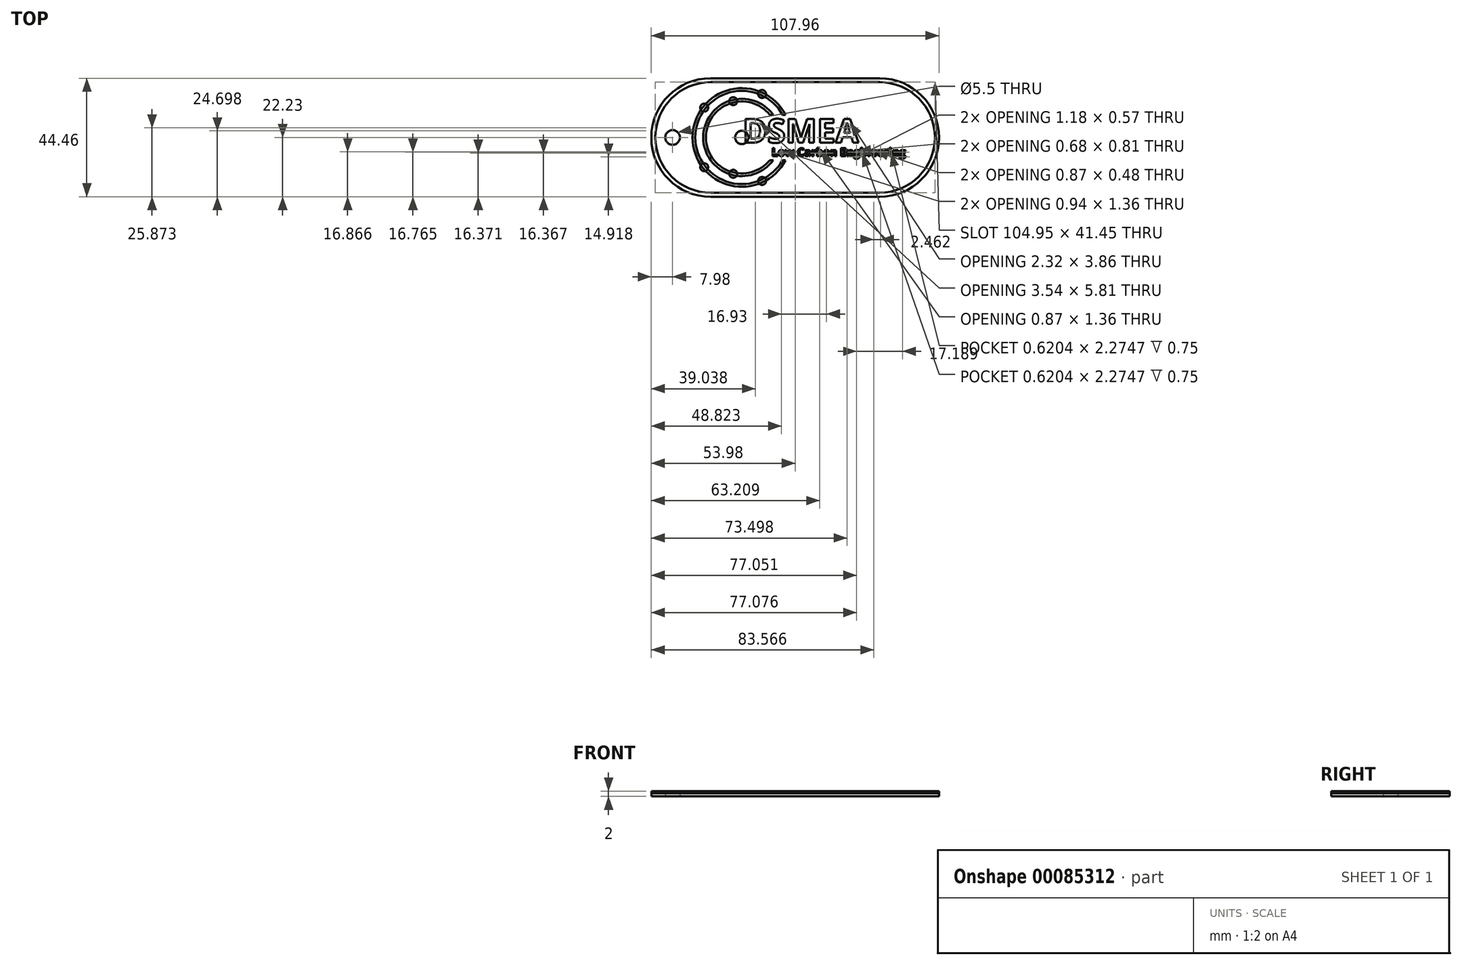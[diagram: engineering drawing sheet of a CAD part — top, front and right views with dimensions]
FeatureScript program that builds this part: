
annotation { "Feature Type Name" : "Feature", "Feature Type Description" : "" }
export const myFeature = defineFeature(function(context is Context, id is Id, definition is map)
    precondition{}
    {
        {
            var Q0;
            Q0=qCreatedBy(makeId("Top.planeOp"),FACE);
            var sketch = newSketch(context, id + "F0", { "sketchPlane" : qUnion([Q0])});
            skLineSegment(sketch, "E0.bottom", {"start": v(31.75, 22.22) * mm, "end": v(-31.75, 22.22) * mm});
            skLineSegment(sketch, "E0.top", {"start": v(31.75, -22.23) * mm, "end": v(-31.75, -22.23) * mm});
            skPoint(sketch, "E0.middle", {"position": v(0, 0) * mm});
            skArc(sketch, "E1", {"start": v(31.75, -22.23) * mm, "mid": v(53.98, 0) * mm, "end": v(31.75, 22.23) * mm});
            skArc(sketch, "E2", {"start": v(-31.75, 22.23) * mm, "mid": v(-53.98, 0) * mm, "end": v(-31.75, -22.23) * mm});
            skSolve(sketch);
        }
        {
            var Q0;
            Q0=qSketchRegion(id+"F0",true);
            extrude(context, id + "F1", {"entities" : qUnion([Q0]), "depth" : 2 * mm});
        }
        {
            var Q0;
            Q0=qCreatedBy(makeId("Top.planeOp"),FACE);
            cPlane(context, id + "F2", {"entities" : qUnion([Q0]), "cplaneType" : CPlaneType.OFFSET, "offset" : 1.25 * mm, "width" : 150 * mm, "height" : 150 * mm});
        }
        {
            var Q0;
            Q0=qCreatedBy(id+"F2.planeOp",FACE);
            var sketch = newSketch(context, id + "F3", { "sketchPlane" : qUnion([Q0])});
            skArc(sketch, "E3", {"start": v(-31.75, 22.23) * mm, "mid": v(-53.98, 0) * mm, "end": v(-31.75, -22.23) * mm});
            skArc(sketch, "E4.0", {"start": v(-31.75, 20.73) * mm, "mid": v(-52.48, 0) * mm, "end": v(-31.75, -20.73) * mm});
            skArc(sketch, "E5.MirrorC", {"start": v(31.75, 22.23) * mm, "mid": v(53.98, 0) * mm, "end": v(31.75, -22.23) * mm});
            skArc(sketch, "E6.MirrorC", {"start": v(31.75, 20.73) * mm, "mid": v(52.48, 0) * mm, "end": v(31.75, -20.73) * mm});
            skLineSegment(sketch, "E7", {"start": v(-31.75, -22.23) * mm, "end": v(31.75, -22.23) * mm});
            skLineSegment(sketch, "E8.MirrorCS", {"start": v(-31.75, 22.23) * mm, "end": v(31.75, 22.23) * mm});
            skLineSegment(sketch, "E9.0", {"start": v(-31.75, 20.73) * mm, "end": v(31.75, 20.73) * mm});
            skLineSegment(sketch, "E10.MirrorCS", {"start": v(-31.75, -20.73) * mm, "end": v(31.75, -20.73) * mm});
            skSolve(sketch);
        }
        {
            var Q0;
            Q0=qSketchRegion(id+"F3",true);
            extrude(context, id + "F4", {"entities" : qUnion([Q0]), "depth" : .75 * mm});
        }
        {
            var Q0;
            Q0=qCreatedBy(id+"F2.planeOp",FACE);
            var sketch = newSketch(context, id + "F5", { "sketchPlane" : qUnion([Q0])});
            skArc(sketch, "E11", {"start": v(-3.57, 8.5) * mm, "mid": v(-38.5, 0) * mm, "end": v(-3.57, -8.5) * mm});
            skArc(sketch, "E12", {"start": v(-4.7, 8.5) * mm, "mid": v(-37.5, 0) * mm, "end": v(-4.7, -8.5) * mm});
            skLineSegment(sketch, "E13.bottom", {"start": v(-3.57, 8.5) * mm, "end": v(-4.7, 8.5) * mm});
            skLineSegment(sketch, "E13.top", {"start": v(-3.57, -8.5) * mm, "end": v(-4.7, -8.5) * mm});
            skPoint(sketch, "E13.middle", {"position": v(0, 0) * mm});
            skSolve(sketch);
        }
        {
            var Q0;
            Q0=qSketchRegion(id+"F5",true);
            extrude(context, id + "F6", {"entities" : qUnion([Q0]), "depth" : .75 * mm});
        }
        {
            var Q0;
            Q0=qCreatedBy(id+"F2.planeOp",FACE);
            var sketch = newSketch(context, id + "F7", { "sketchPlane" : qUnion([Q0])});
            skArc(sketch, "E14", {"start": v(-8.25, 8.5) * mm, "mid": v(-34.5, 0) * mm, "end": v(-8.25, -8.5) * mm});
            skArc(sketch, "E15", {"start": v(-9.51, 8.5) * mm, "mid": v(-33.5, 0) * mm, "end": v(-9.51, -8.5) * mm});
            skLineSegment(sketch, "E16.bottom", {"start": v(-8.25, 8.5) * mm, "end": v(-9.51, 8.5) * mm});
            skLineSegment(sketch, "E16.top", {"start": v(-8.25, -8.5) * mm, "end": v(-9.51, -8.5) * mm});
            skPoint(sketch, "E16.middle", {"position": v(0, 0) * mm});
            skSolve(sketch);
        }
        {
            var Q0;
            Q0=qSketchRegion(id+"F7",true);
            extrude(context, id + "F8", {"entities" : qUnion([Q0]), "depth" : .75 * mm});
        }
        {
            var Q0;
            Q0=qCreatedBy(id+"F2.planeOp",FACE);
            var sketch = newSketch(context, id + "F9", { "sketchPlane" : qUnion([Q0])});
            skCircle(sketch, "E17", {"center": v(-20, 0) * mm, "radius": 2.5 * mm});
            skCircle(sketch, "E18", {"center": v(-20, 0) * mm, "radius": 18 * mm, "construction": true});
            skCircle(sketch, "E19", {"center": v(-20, 0) * mm, "radius": 14 * mm, "construction": true});
            skLineSegment(sketch, "E20", {"start": v(-20, 0) * mm, "end": v(-12.4, 16.31) * mm, "construction": true});
            skLineSegment(sketch, "E21", {"start": v(-20, 0) * mm, "end": v(-12.4, -16.31) * mm, "construction": true});
            skCircle(sketch, "E22", {"center": v(-12.4, 16.31) * mm, "radius": 1.5 * mm});
            skCircle(sketch, "E23.1.0", {"center": v(-34.12, 11.16) * mm, "radius": 1.5 * mm});
            skCircle(sketch, "E23.2.0", {"center": v(-34.12, -11.16) * mm, "radius": 1.5 * mm});
            skCircle(sketch, "E23.3.0", {"center": v(-12.4, -16.31) * mm, "radius": 1.5 * mm});
            skLineSegment(sketch, "E24", {"start": v(-34.12, 11.16) * mm, "end": v(-20, 0) * mm, "construction": true});
            skLineSegment(sketch, "E25", {"start": v(-23.23, 13.62) * mm, "end": v(-20, 0) * mm, "construction": true});
            skCircle(sketch, "E26", {"center": v(-23.23, 13.62) * mm, "radius": 1.5 * mm});
            skCircle(sketch, "E27.MirrorC", {"center": v(-23.23, -13.62) * mm, "radius": 1.5 * mm});
            skSolve(sketch);
        }
        {
            var Q0;
            Q0=qSketchRegion(id+"F9",true);
            extrude(context, id + "F10", {"entities" : qUnion([Q0]), "depth" : .75 * mm});
        }
        {
            var Q0;
            Q0=qCreatedBy(id+"F2.planeOp",FACE);
            var sketch = newSketch(context, id + "F11", { "sketchPlane" : qUnion([Q0])});
            skText(sketch, "E28", { "text": "DSMEA", "fontName": "OpenSans-Bold.ttf"});
            const initialGuessF11  = {"E28": [-0.01973, -0.002, 1, 0, 0.009]};
            skSetInitialGuess(sketch, initialGuessF11);
            skSolve(sketch);
        }
        {
            var Q0;
            Q0=qSketchRegion(id+"F11",true);
            extrude(context, id + "F12", {"entities" : qUnion([Q0]), "depth" : .75 * mm});
        }
        {
            var Q0;
            Q0=qCreatedBy(id+"F2.planeOp",FACE);
            var sketch = newSketch(context, id + "F13", { "sketchPlane" : qUnion([Q0])});
            skText(sketch, "E29", { "text": "Low Carbon Engineering", "fontName": "OpenSans-Bold.ttf"});
            const initialGuessF13  = {"E29": [-0.0088, -0.007, 1, 0, 0.003]};
            skSetInitialGuess(sketch, initialGuessF13);
            skSolve(sketch);
        }
        {
            var Q0;
            Q0=qSketchRegion(id+"F13",true);
            extrude(context, id + "F14", {"entities" : qUnion([Q0]), "depth" : .75 * mm});
        }
        {
            var Q0;
            Q0=makeQuery(id+"F4.opExtrude","SWEPT_BODY",BODY,{"disambiguationData":[OSD([sQuery(id+"F3.wireOp",EDGE,"E3"),sQuery(id+"F3.wireOp",EDGE,"E4.0"),sQuery(id+"F3.wireOp",EDGE,"E5.MirrorC"),sQuery(id+"F3.wireOp",EDGE,"E6.MirrorC"),sQuery(id+"F3.wireOp",EDGE,"E7"),sQuery(id+"F3.wireOp",EDGE,"E8.MirrorCS"),sQuery(id+"F3.wireOp",EDGE,"E9.0"),sQuery(id+"F3.wireOp",EDGE,"E10.MirrorCS")])]});
            var Q1;
            Q1=makeQuery(id+"F1.opExtrude","SWEPT_BODY",BODY,{"disambiguationData":[OSD([sQuery(id+"F0.wireOp",EDGE,"E0.bottom"),sQuery(id+"F0.wireOp",EDGE,"E0.top"),sQuery(id+"F0.wireOp",EDGE,"E1"),sQuery(id+"F0.wireOp",EDGE,"E2")])]});
            booleanBodies(context, id + "F15", {"operationType" : BooleanOperationType.SUBTRACTION, "tools" : qUnion([Q0]), "targets" : qUnion([Q1]), "keepTools" : true});
        }
        {
            var Q0;
            Q0=makeQuery(id+"F12.opExtrude","SWEPT_BODY",BODY,{"disambiguationData":[OSD([sQuery(id+"F11.wireOp",EDGE,"E28.sketch_text.stroke-0"),sQuery(id+"F11.wireOp",EDGE,"E28.sketch_text.stroke-1"),sQuery(id+"F11.wireOp",EDGE,"E28.sketch_text.stroke-2"),sQuery(id+"F11.wireOp",EDGE,"E28.sketch_text.stroke-3"),sQuery(id+"F11.wireOp",EDGE,"E28.sketch_text.stroke-4"),sQuery(id+"F11.wireOp",EDGE,"E28.sketch_text.stroke-5"),sQuery(id+"F11.wireOp",EDGE,"E28.sketch_text.stroke-6"),sQuery(id+"F11.wireOp",EDGE,"E28.sketch_text.stroke-7"),sQuery(id+"F11.wireOp",EDGE,"E28.sketch_text.stroke-8"),sQuery(id+"F11.wireOp",EDGE,"E28.sketch_text.stroke-9"),sQuery(id+"F11.wireOp",EDGE,"E28.sketch_text.stroke-10"),sQuery(id+"F11.wireOp",EDGE,"E28.sketch_text.stroke-11")])]});
            var Q1;
            Q1=makeQuery(id+"F12.opExtrude","SWEPT_BODY",BODY,{"disambiguationData":[OSD([sQuery(id+"F11.wireOp",EDGE,"E28.sketch_text.stroke-12"),sQuery(id+"F11.wireOp",EDGE,"E28.sketch_text.stroke-13"),sQuery(id+"F11.wireOp",EDGE,"E28.sketch_text.stroke-14"),sQuery(id+"F11.wireOp",EDGE,"E28.sketch_text.stroke-15"),sQuery(id+"F11.wireOp",EDGE,"E28.sketch_text.stroke-16"),sQuery(id+"F11.wireOp",EDGE,"E28.sketch_text.stroke-17"),sQuery(id+"F11.wireOp",EDGE,"E28.sketch_text.stroke-18"),sQuery(id+"F11.wireOp",EDGE,"E28.sketch_text.stroke-19"),sQuery(id+"F11.wireOp",EDGE,"E28.sketch_text.stroke-20"),sQuery(id+"F11.wireOp",EDGE,"E28.sketch_text.stroke-21"),sQuery(id+"F11.wireOp",EDGE,"E28.sketch_text.stroke-22"),sQuery(id+"F11.wireOp",EDGE,"E28.sketch_text.stroke-23"),sQuery(id+"F11.wireOp",EDGE,"E28.sketch_text.stroke-24"),sQuery(id+"F11.wireOp",EDGE,"E28.sketch_text.stroke-25"),sQuery(id+"F11.wireOp",EDGE,"E28.sketch_text.stroke-26"),sQuery(id+"F11.wireOp",EDGE,"E28.sketch_text.stroke-27"),sQuery(id+"F11.wireOp",EDGE,"E28.sketch_text.stroke-28"),sQuery(id+"F11.wireOp",EDGE,"E28.sketch_text.stroke-29"),sQuery(id+"F11.wireOp",EDGE,"E28.sketch_text.stroke-30"),sQuery(id+"F11.wireOp",EDGE,"E28.sketch_text.stroke-31"),sQuery(id+"F11.wireOp",EDGE,"E28.sketch_text.stroke-32"),sQuery(id+"F11.wireOp",EDGE,"E28.sketch_text.stroke-33"),sQuery(id+"F11.wireOp",EDGE,"E28.sketch_text.stroke-34"),sQuery(id+"F11.wireOp",EDGE,"E28.sketch_text.stroke-35"),sQuery(id+"F11.wireOp",EDGE,"E28.sketch_text.stroke-36"),sQuery(id+"F11.wireOp",EDGE,"E28.sketch_text.stroke-37"),sQuery(id+"F11.wireOp",EDGE,"E28.sketch_text.stroke-38"),sQuery(id+"F11.wireOp",EDGE,"E28.sketch_text.stroke-39")])]});
            var Q2;
            Q2=makeQuery(id+"F12.opExtrude","SWEPT_BODY",BODY,{"disambiguationData":[OSD([sQuery(id+"F11.wireOp",EDGE,"E28.sketch_text.stroke-40"),sQuery(id+"F11.wireOp",EDGE,"E28.sketch_text.stroke-41"),sQuery(id+"F11.wireOp",EDGE,"E28.sketch_text.stroke-42"),sQuery(id+"F11.wireOp",EDGE,"E28.sketch_text.stroke-43"),sQuery(id+"F11.wireOp",EDGE,"E28.sketch_text.stroke-44"),sQuery(id+"F11.wireOp",EDGE,"E28.sketch_text.stroke-45"),sQuery(id+"F11.wireOp",EDGE,"E28.sketch_text.stroke-46"),sQuery(id+"F11.wireOp",EDGE,"E28.sketch_text.stroke-47"),sQuery(id+"F11.wireOp",EDGE,"E28.sketch_text.stroke-48"),sQuery(id+"F11.wireOp",EDGE,"E28.sketch_text.stroke-49"),sQuery(id+"F11.wireOp",EDGE,"E28.sketch_text.stroke-50"),sQuery(id+"F11.wireOp",EDGE,"E28.sketch_text.stroke-51"),sQuery(id+"F11.wireOp",EDGE,"E28.sketch_text.stroke-52"),sQuery(id+"F11.wireOp",EDGE,"E28.sketch_text.stroke-53"),sQuery(id+"F11.wireOp",EDGE,"E28.sketch_text.stroke-54"),sQuery(id+"F11.wireOp",EDGE,"E28.sketch_text.stroke-55"),sQuery(id+"F11.wireOp",EDGE,"E28.sketch_text.stroke-56"),sQuery(id+"F11.wireOp",EDGE,"E28.sketch_text.stroke-57"),sQuery(id+"F11.wireOp",EDGE,"E28.sketch_text.stroke-58")])]});
            var Q3;
            Q3=makeQuery(id+"F12.opExtrude","SWEPT_BODY",BODY,{"disambiguationData":[OSD([sQuery(id+"F11.wireOp",EDGE,"E28.sketch_text.stroke-59"),sQuery(id+"F11.wireOp",EDGE,"E28.sketch_text.stroke-60"),sQuery(id+"F11.wireOp",EDGE,"E28.sketch_text.stroke-61"),sQuery(id+"F11.wireOp",EDGE,"E28.sketch_text.stroke-62"),sQuery(id+"F11.wireOp",EDGE,"E28.sketch_text.stroke-63"),sQuery(id+"F11.wireOp",EDGE,"E28.sketch_text.stroke-64"),sQuery(id+"F11.wireOp",EDGE,"E28.sketch_text.stroke-65"),sQuery(id+"F11.wireOp",EDGE,"E28.sketch_text.stroke-66"),sQuery(id+"F11.wireOp",EDGE,"E28.sketch_text.stroke-67"),sQuery(id+"F11.wireOp",EDGE,"E28.sketch_text.stroke-68"),sQuery(id+"F11.wireOp",EDGE,"E28.sketch_text.stroke-69"),sQuery(id+"F11.wireOp",EDGE,"E28.sketch_text.stroke-70")])]});
            var Q4;
            Q4=makeQuery(id+"F12.opExtrude","SWEPT_BODY",BODY,{"disambiguationData":[OSD([sQuery(id+"F11.wireOp",EDGE,"E28.sketch_text.stroke-71"),sQuery(id+"F11.wireOp",EDGE,"E28.sketch_text.stroke-72"),sQuery(id+"F11.wireOp",EDGE,"E28.sketch_text.stroke-73"),sQuery(id+"F11.wireOp",EDGE,"E28.sketch_text.stroke-74"),sQuery(id+"F11.wireOp",EDGE,"E28.sketch_text.stroke-75"),sQuery(id+"F11.wireOp",EDGE,"E28.sketch_text.stroke-76"),sQuery(id+"F11.wireOp",EDGE,"E28.sketch_text.stroke-77"),sQuery(id+"F11.wireOp",EDGE,"E28.sketch_text.stroke-78"),sQuery(id+"F11.wireOp",EDGE,"E28.sketch_text.stroke-79"),sQuery(id+"F11.wireOp",EDGE,"E28.sketch_text.stroke-80"),sQuery(id+"F11.wireOp",EDGE,"E28.sketch_text.stroke-81"),sQuery(id+"F11.wireOp",EDGE,"E28.sketch_text.stroke-82")])]});
            var Q5;
            Q5=makeQuery(id+"F1.opExtrude","SWEPT_BODY",BODY,{"disambiguationData":[OSD([sQuery(id+"F0.wireOp",EDGE,"E0.bottom"),sQuery(id+"F0.wireOp",EDGE,"E0.top"),sQuery(id+"F0.wireOp",EDGE,"E1"),sQuery(id+"F0.wireOp",EDGE,"E2")])]});
            booleanBodies(context, id + "F16", {"operationType" : BooleanOperationType.SUBTRACTION, "tools" : qUnion([Q0, Q1, Q2, Q3, Q4]), "targets" : qUnion([Q5]), "keepTools" : true});
        }
        {
            var Q0;
            Q0=makeQuery(id+"F14.opExtrude","SWEPT_BODY",BODY,{"disambiguationData":[OSD([sQuery(id+"F13.wireOp",EDGE,"E29.sketch_text.stroke-0"),sQuery(id+"F13.wireOp",EDGE,"E29.sketch_text.stroke-1"),sQuery(id+"F13.wireOp",EDGE,"E29.sketch_text.stroke-2"),sQuery(id+"F13.wireOp",EDGE,"E29.sketch_text.stroke-3"),sQuery(id+"F13.wireOp",EDGE,"E29.sketch_text.stroke-4"),sQuery(id+"F13.wireOp",EDGE,"E29.sketch_text.stroke-5")])]});
            var Q1;
            Q1=makeQuery(id+"F14.opExtrude","SWEPT_BODY",BODY,{"disambiguationData":[OSD([sQuery(id+"F13.wireOp",EDGE,"E29.sketch_text.stroke-6"),sQuery(id+"F13.wireOp",EDGE,"E29.sketch_text.stroke-7"),sQuery(id+"F13.wireOp",EDGE,"E29.sketch_text.stroke-8"),sQuery(id+"F13.wireOp",EDGE,"E29.sketch_text.stroke-9"),sQuery(id+"F13.wireOp",EDGE,"E29.sketch_text.stroke-10"),sQuery(id+"F13.wireOp",EDGE,"E29.sketch_text.stroke-11"),sQuery(id+"F13.wireOp",EDGE,"E29.sketch_text.stroke-12"),sQuery(id+"F13.wireOp",EDGE,"E29.sketch_text.stroke-13"),sQuery(id+"F13.wireOp",EDGE,"E29.sketch_text.stroke-14"),sQuery(id+"F13.wireOp",EDGE,"E29.sketch_text.stroke-15"),sQuery(id+"F13.wireOp",EDGE,"E29.sketch_text.stroke-16"),sQuery(id+"F13.wireOp",EDGE,"E29.sketch_text.stroke-17"),sQuery(id+"F13.wireOp",EDGE,"E29.sketch_text.stroke-18"),sQuery(id+"F13.wireOp",EDGE,"E29.sketch_text.stroke-19"),sQuery(id+"F13.wireOp",EDGE,"E29.sketch_text.stroke-20"),sQuery(id+"F13.wireOp",EDGE,"E29.sketch_text.stroke-21"),sQuery(id+"F13.wireOp",EDGE,"E29.sketch_text.stroke-22"),sQuery(id+"F13.wireOp",EDGE,"E29.sketch_text.stroke-23")])]});
            var Q2;
            Q2=makeQuery(id+"F14.opExtrude","SWEPT_BODY",BODY,{"disambiguationData":[OSD([sQuery(id+"F13.wireOp",EDGE,"E29.sketch_text.stroke-24"),sQuery(id+"F13.wireOp",EDGE,"E29.sketch_text.stroke-25"),sQuery(id+"F13.wireOp",EDGE,"E29.sketch_text.stroke-26"),sQuery(id+"F13.wireOp",EDGE,"E29.sketch_text.stroke-27"),sQuery(id+"F13.wireOp",EDGE,"E29.sketch_text.stroke-28"),sQuery(id+"F13.wireOp",EDGE,"E29.sketch_text.stroke-29"),sQuery(id+"F13.wireOp",EDGE,"E29.sketch_text.stroke-30"),sQuery(id+"F13.wireOp",EDGE,"E29.sketch_text.stroke-31"),sQuery(id+"F13.wireOp",EDGE,"E29.sketch_text.stroke-32"),sQuery(id+"F13.wireOp",EDGE,"E29.sketch_text.stroke-33"),sQuery(id+"F13.wireOp",EDGE,"E29.sketch_text.stroke-34"),sQuery(id+"F13.wireOp",EDGE,"E29.sketch_text.stroke-35"),sQuery(id+"F13.wireOp",EDGE,"E29.sketch_text.stroke-36"),sQuery(id+"F13.wireOp",EDGE,"E29.sketch_text.stroke-37"),sQuery(id+"F13.wireOp",EDGE,"E29.sketch_text.stroke-38"),sQuery(id+"F13.wireOp",EDGE,"E29.sketch_text.stroke-39"),sQuery(id+"F13.wireOp",EDGE,"E29.sketch_text.stroke-40"),sQuery(id+"F13.wireOp",EDGE,"E29.sketch_text.stroke-41"),sQuery(id+"F13.wireOp",EDGE,"E29.sketch_text.stroke-42"),sQuery(id+"F13.wireOp",EDGE,"E29.sketch_text.stroke-43"),sQuery(id+"F13.wireOp",EDGE,"E29.sketch_text.stroke-44"),sQuery(id+"F13.wireOp",EDGE,"E29.sketch_text.stroke-45"),sQuery(id+"F13.wireOp",EDGE,"E29.sketch_text.stroke-46"),sQuery(id+"F13.wireOp",EDGE,"E29.sketch_text.stroke-47"),sQuery(id+"F13.wireOp",EDGE,"E29.sketch_text.stroke-48"),sQuery(id+"F13.wireOp",EDGE,"E29.sketch_text.stroke-49")])]});
            var Q3;
            Q3=makeQuery(id+"F14.opExtrude","SWEPT_BODY",BODY,{"disambiguationData":[OSD([sQuery(id+"F13.wireOp",EDGE,"E29.sketch_text.stroke-50"),sQuery(id+"F13.wireOp",EDGE,"E29.sketch_text.stroke-51"),sQuery(id+"F13.wireOp",EDGE,"E29.sketch_text.stroke-52"),sQuery(id+"F13.wireOp",EDGE,"E29.sketch_text.stroke-53"),sQuery(id+"F13.wireOp",EDGE,"E29.sketch_text.stroke-54"),sQuery(id+"F13.wireOp",EDGE,"E29.sketch_text.stroke-55"),sQuery(id+"F13.wireOp",EDGE,"E29.sketch_text.stroke-56"),sQuery(id+"F13.wireOp",EDGE,"E29.sketch_text.stroke-57"),sQuery(id+"F13.wireOp",EDGE,"E29.sketch_text.stroke-58"),sQuery(id+"F13.wireOp",EDGE,"E29.sketch_text.stroke-59"),sQuery(id+"F13.wireOp",EDGE,"E29.sketch_text.stroke-60"),sQuery(id+"F13.wireOp",EDGE,"E29.sketch_text.stroke-61"),sQuery(id+"F13.wireOp",EDGE,"E29.sketch_text.stroke-62"),sQuery(id+"F13.wireOp",EDGE,"E29.sketch_text.stroke-63"),sQuery(id+"F13.wireOp",EDGE,"E29.sketch_text.stroke-64")])]});
            var Q4;
            Q4=makeQuery(id+"F14.opExtrude","SWEPT_BODY",BODY,{"disambiguationData":[OSD([sQuery(id+"F13.wireOp",EDGE,"E29.sketch_text.stroke-65"),sQuery(id+"F13.wireOp",EDGE,"E29.sketch_text.stroke-66"),sQuery(id+"F13.wireOp",EDGE,"E29.sketch_text.stroke-67"),sQuery(id+"F13.wireOp",EDGE,"E29.sketch_text.stroke-68"),sQuery(id+"F13.wireOp",EDGE,"E29.sketch_text.stroke-69"),sQuery(id+"F13.wireOp",EDGE,"E29.sketch_text.stroke-70"),sQuery(id+"F13.wireOp",EDGE,"E29.sketch_text.stroke-71"),sQuery(id+"F13.wireOp",EDGE,"E29.sketch_text.stroke-72"),sQuery(id+"F13.wireOp",EDGE,"E29.sketch_text.stroke-73"),sQuery(id+"F13.wireOp",EDGE,"E29.sketch_text.stroke-74"),sQuery(id+"F13.wireOp",EDGE,"E29.sketch_text.stroke-75"),sQuery(id+"F13.wireOp",EDGE,"E29.sketch_text.stroke-76"),sQuery(id+"F13.wireOp",EDGE,"E29.sketch_text.stroke-77"),sQuery(id+"F13.wireOp",EDGE,"E29.sketch_text.stroke-78"),sQuery(id+"F13.wireOp",EDGE,"E29.sketch_text.stroke-79"),sQuery(id+"F13.wireOp",EDGE,"E29.sketch_text.stroke-80"),sQuery(id+"F13.wireOp",EDGE,"E29.sketch_text.stroke-81"),sQuery(id+"F13.wireOp",EDGE,"E29.sketch_text.stroke-82"),sQuery(id+"F13.wireOp",EDGE,"E29.sketch_text.stroke-83"),sQuery(id+"F13.wireOp",EDGE,"E29.sketch_text.stroke-84"),sQuery(id+"F13.wireOp",EDGE,"E29.sketch_text.stroke-85"),sQuery(id+"F13.wireOp",EDGE,"E29.sketch_text.stroke-86"),sQuery(id+"F13.wireOp",EDGE,"E29.sketch_text.stroke-87"),sQuery(id+"F13.wireOp",EDGE,"E29.sketch_text.stroke-88"),sQuery(id+"F13.wireOp",EDGE,"E29.sketch_text.stroke-89")])]});
            var Q5;
            Q5=makeQuery(id+"F14.opExtrude","SWEPT_BODY",BODY,{"disambiguationData":[OSD([sQuery(id+"F13.wireOp",EDGE,"E29.sketch_text.stroke-90"),sQuery(id+"F13.wireOp",EDGE,"E29.sketch_text.stroke-91"),sQuery(id+"F13.wireOp",EDGE,"E29.sketch_text.stroke-92"),sQuery(id+"F13.wireOp",EDGE,"E29.sketch_text.stroke-93"),sQuery(id+"F13.wireOp",EDGE,"E29.sketch_text.stroke-94"),sQuery(id+"F13.wireOp",EDGE,"E29.sketch_text.stroke-95"),sQuery(id+"F13.wireOp",EDGE,"E29.sketch_text.stroke-96"),sQuery(id+"F13.wireOp",EDGE,"E29.sketch_text.stroke-97"),sQuery(id+"F13.wireOp",EDGE,"E29.sketch_text.stroke-98"),sQuery(id+"F13.wireOp",EDGE,"E29.sketch_text.stroke-99"),sQuery(id+"F13.wireOp",EDGE,"E29.sketch_text.stroke-100"),sQuery(id+"F13.wireOp",EDGE,"E29.sketch_text.stroke-101"),sQuery(id+"F13.wireOp",EDGE,"E29.sketch_text.stroke-102")])]});
            var Q6;
            Q6=makeQuery(id+"F14.opExtrude","SWEPT_BODY",BODY,{"disambiguationData":[OSD([sQuery(id+"F13.wireOp",EDGE,"E29.sketch_text.stroke-103"),sQuery(id+"F13.wireOp",EDGE,"E29.sketch_text.stroke-104"),sQuery(id+"F13.wireOp",EDGE,"E29.sketch_text.stroke-105"),sQuery(id+"F13.wireOp",EDGE,"E29.sketch_text.stroke-106"),sQuery(id+"F13.wireOp",EDGE,"E29.sketch_text.stroke-107"),sQuery(id+"F13.wireOp",EDGE,"E29.sketch_text.stroke-108"),sQuery(id+"F13.wireOp",EDGE,"E29.sketch_text.stroke-109"),sQuery(id+"F13.wireOp",EDGE,"E29.sketch_text.stroke-110"),sQuery(id+"F13.wireOp",EDGE,"E29.sketch_text.stroke-111"),sQuery(id+"F13.wireOp",EDGE,"E29.sketch_text.stroke-112"),sQuery(id+"F13.wireOp",EDGE,"E29.sketch_text.stroke-113"),sQuery(id+"F13.wireOp",EDGE,"E29.sketch_text.stroke-114"),sQuery(id+"F13.wireOp",EDGE,"E29.sketch_text.stroke-115"),sQuery(id+"F13.wireOp",EDGE,"E29.sketch_text.stroke-116"),sQuery(id+"F13.wireOp",EDGE,"E29.sketch_text.stroke-117"),sQuery(id+"F13.wireOp",EDGE,"E29.sketch_text.stroke-118"),sQuery(id+"F13.wireOp",EDGE,"E29.sketch_text.stroke-119"),sQuery(id+"F13.wireOp",EDGE,"E29.sketch_text.stroke-120"),sQuery(id+"F13.wireOp",EDGE,"E29.sketch_text.stroke-121"),sQuery(id+"F13.wireOp",EDGE,"E29.sketch_text.stroke-122"),sQuery(id+"F13.wireOp",EDGE,"E29.sketch_text.stroke-123"),sQuery(id+"F13.wireOp",EDGE,"E29.sketch_text.stroke-124"),sQuery(id+"F13.wireOp",EDGE,"E29.sketch_text.stroke-125")])]});
            var Q7;
            Q7=makeQuery(id+"F14.opExtrude","SWEPT_BODY",BODY,{"disambiguationData":[OSD([sQuery(id+"F13.wireOp",EDGE,"E29.sketch_text.stroke-126"),sQuery(id+"F13.wireOp",EDGE,"E29.sketch_text.stroke-127"),sQuery(id+"F13.wireOp",EDGE,"E29.sketch_text.stroke-128"),sQuery(id+"F13.wireOp",EDGE,"E29.sketch_text.stroke-129"),sQuery(id+"F13.wireOp",EDGE,"E29.sketch_text.stroke-130"),sQuery(id+"F13.wireOp",EDGE,"E29.sketch_text.stroke-131"),sQuery(id+"F13.wireOp",EDGE,"E29.sketch_text.stroke-132"),sQuery(id+"F13.wireOp",EDGE,"E29.sketch_text.stroke-133"),sQuery(id+"F13.wireOp",EDGE,"E29.sketch_text.stroke-134"),sQuery(id+"F13.wireOp",EDGE,"E29.sketch_text.stroke-135"),sQuery(id+"F13.wireOp",EDGE,"E29.sketch_text.stroke-136"),sQuery(id+"F13.wireOp",EDGE,"E29.sketch_text.stroke-137"),sQuery(id+"F13.wireOp",EDGE,"E29.sketch_text.stroke-138"),sQuery(id+"F13.wireOp",EDGE,"E29.sketch_text.stroke-139"),sQuery(id+"F13.wireOp",EDGE,"E29.sketch_text.stroke-140"),sQuery(id+"F13.wireOp",EDGE,"E29.sketch_text.stroke-141"),sQuery(id+"F13.wireOp",EDGE,"E29.sketch_text.stroke-142"),sQuery(id+"F13.wireOp",EDGE,"E29.sketch_text.stroke-143")])]});
            var Q8;
            Q8=makeQuery(id+"F14.opExtrude","SWEPT_BODY",BODY,{"disambiguationData":[OSD([sQuery(id+"F13.wireOp",EDGE,"E29.sketch_text.stroke-144"),sQuery(id+"F13.wireOp",EDGE,"E29.sketch_text.stroke-145"),sQuery(id+"F13.wireOp",EDGE,"E29.sketch_text.stroke-146"),sQuery(id+"F13.wireOp",EDGE,"E29.sketch_text.stroke-147"),sQuery(id+"F13.wireOp",EDGE,"E29.sketch_text.stroke-148"),sQuery(id+"F13.wireOp",EDGE,"E29.sketch_text.stroke-149"),sQuery(id+"F13.wireOp",EDGE,"E29.sketch_text.stroke-150"),sQuery(id+"F13.wireOp",EDGE,"E29.sketch_text.stroke-151"),sQuery(id+"F13.wireOp",EDGE,"E29.sketch_text.stroke-152"),sQuery(id+"F13.wireOp",EDGE,"E29.sketch_text.stroke-153"),sQuery(id+"F13.wireOp",EDGE,"E29.sketch_text.stroke-154"),sQuery(id+"F13.wireOp",EDGE,"E29.sketch_text.stroke-155"),sQuery(id+"F13.wireOp",EDGE,"E29.sketch_text.stroke-156"),sQuery(id+"F13.wireOp",EDGE,"E29.sketch_text.stroke-157"),sQuery(id+"F13.wireOp",EDGE,"E29.sketch_text.stroke-158"),sQuery(id+"F13.wireOp",EDGE,"E29.sketch_text.stroke-159"),sQuery(id+"F13.wireOp",EDGE,"E29.sketch_text.stroke-160")])]});
            var Q9;
            Q9=makeQuery(id+"F14.opExtrude","SWEPT_BODY",BODY,{"disambiguationData":[OSD([sQuery(id+"F13.wireOp",EDGE,"E29.sketch_text.stroke-161"),sQuery(id+"F13.wireOp",EDGE,"E29.sketch_text.stroke-162"),sQuery(id+"F13.wireOp",EDGE,"E29.sketch_text.stroke-163"),sQuery(id+"F13.wireOp",EDGE,"E29.sketch_text.stroke-164"),sQuery(id+"F13.wireOp",EDGE,"E29.sketch_text.stroke-165"),sQuery(id+"F13.wireOp",EDGE,"E29.sketch_text.stroke-166"),sQuery(id+"F13.wireOp",EDGE,"E29.sketch_text.stroke-167"),sQuery(id+"F13.wireOp",EDGE,"E29.sketch_text.stroke-168"),sQuery(id+"F13.wireOp",EDGE,"E29.sketch_text.stroke-169"),sQuery(id+"F13.wireOp",EDGE,"E29.sketch_text.stroke-170"),sQuery(id+"F13.wireOp",EDGE,"E29.sketch_text.stroke-171"),sQuery(id+"F13.wireOp",EDGE,"E29.sketch_text.stroke-172")])]});
            var Q10;
            Q10=makeQuery(id+"F14.opExtrude","SWEPT_BODY",BODY,{"disambiguationData":[OSD([sQuery(id+"F13.wireOp",EDGE,"E29.sketch_text.stroke-173"),sQuery(id+"F13.wireOp",EDGE,"E29.sketch_text.stroke-174"),sQuery(id+"F13.wireOp",EDGE,"E29.sketch_text.stroke-175"),sQuery(id+"F13.wireOp",EDGE,"E29.sketch_text.stroke-176"),sQuery(id+"F13.wireOp",EDGE,"E29.sketch_text.stroke-177"),sQuery(id+"F13.wireOp",EDGE,"E29.sketch_text.stroke-178"),sQuery(id+"F13.wireOp",EDGE,"E29.sketch_text.stroke-179"),sQuery(id+"F13.wireOp",EDGE,"E29.sketch_text.stroke-180"),sQuery(id+"F13.wireOp",EDGE,"E29.sketch_text.stroke-181"),sQuery(id+"F13.wireOp",EDGE,"E29.sketch_text.stroke-182"),sQuery(id+"F13.wireOp",EDGE,"E29.sketch_text.stroke-183"),sQuery(id+"F13.wireOp",EDGE,"E29.sketch_text.stroke-184"),sQuery(id+"F13.wireOp",EDGE,"E29.sketch_text.stroke-185"),sQuery(id+"F13.wireOp",EDGE,"E29.sketch_text.stroke-186"),sQuery(id+"F13.wireOp",EDGE,"E29.sketch_text.stroke-187"),sQuery(id+"F13.wireOp",EDGE,"E29.sketch_text.stroke-188"),sQuery(id+"F13.wireOp",EDGE,"E29.sketch_text.stroke-189")])]});
            var Q11;
            Q11=makeQuery(id+"F14.opExtrude","SWEPT_BODY",BODY,{"disambiguationData":[OSD([sQuery(id+"F13.wireOp",EDGE,"E29.sketch_text.stroke-190"),sQuery(id+"F13.wireOp",EDGE,"E29.sketch_text.stroke-191"),sQuery(id+"F13.wireOp",EDGE,"E29.sketch_text.stroke-192"),sQuery(id+"F13.wireOp",EDGE,"E29.sketch_text.stroke-193"),sQuery(id+"F13.wireOp",EDGE,"E29.sketch_text.stroke-194"),sQuery(id+"F13.wireOp",EDGE,"E29.sketch_text.stroke-195"),sQuery(id+"F13.wireOp",EDGE,"E29.sketch_text.stroke-196"),sQuery(id+"F13.wireOp",EDGE,"E29.sketch_text.stroke-197"),sQuery(id+"F13.wireOp",EDGE,"E29.sketch_text.stroke-198"),sQuery(id+"F13.wireOp",EDGE,"E29.sketch_text.stroke-199"),sQuery(id+"F13.wireOp",EDGE,"E29.sketch_text.stroke-200"),sQuery(id+"F13.wireOp",EDGE,"E29.sketch_text.stroke-201"),sQuery(id+"F13.wireOp",EDGE,"E29.sketch_text.stroke-202"),sQuery(id+"F13.wireOp",EDGE,"E29.sketch_text.stroke-203"),sQuery(id+"F13.wireOp",EDGE,"E29.sketch_text.stroke-204"),sQuery(id+"F13.wireOp",EDGE,"E29.sketch_text.stroke-205"),sQuery(id+"F13.wireOp",EDGE,"E29.sketch_text.stroke-206"),sQuery(id+"F13.wireOp",EDGE,"E29.sketch_text.stroke-207"),sQuery(id+"F13.wireOp",EDGE,"E29.sketch_text.stroke-208"),sQuery(id+"F13.wireOp",EDGE,"E29.sketch_text.stroke-209"),sQuery(id+"F13.wireOp",EDGE,"E29.sketch_text.stroke-210"),sQuery(id+"F13.wireOp",EDGE,"E29.sketch_text.stroke-211"),sQuery(id+"F13.wireOp",EDGE,"E29.sketch_text.stroke-212"),sQuery(id+"F13.wireOp",EDGE,"E29.sketch_text.stroke-213"),sQuery(id+"F13.wireOp",EDGE,"E29.sketch_text.stroke-214"),sQuery(id+"F13.wireOp",EDGE,"E29.sketch_text.stroke-215"),sQuery(id+"F13.wireOp",EDGE,"E29.sketch_text.stroke-216"),sQuery(id+"F13.wireOp",EDGE,"E29.sketch_text.stroke-217"),sQuery(id+"F13.wireOp",EDGE,"E29.sketch_text.stroke-218"),sQuery(id+"F13.wireOp",EDGE,"E29.sketch_text.stroke-219"),sQuery(id+"F13.wireOp",EDGE,"E29.sketch_text.stroke-220"),sQuery(id+"F13.wireOp",EDGE,"E29.sketch_text.stroke-221"),sQuery(id+"F13.wireOp",EDGE,"E29.sketch_text.stroke-222"),sQuery(id+"F13.wireOp",EDGE,"E29.sketch_text.stroke-223"),sQuery(id+"F13.wireOp",EDGE,"E29.sketch_text.stroke-224"),sQuery(id+"F13.wireOp",EDGE,"E29.sketch_text.stroke-225"),sQuery(id+"F13.wireOp",EDGE,"E29.sketch_text.stroke-226"),sQuery(id+"F13.wireOp",EDGE,"E29.sketch_text.stroke-227"),sQuery(id+"F13.wireOp",EDGE,"E29.sketch_text.stroke-228"),sQuery(id+"F13.wireOp",EDGE,"E29.sketch_text.stroke-229"),sQuery(id+"F13.wireOp",EDGE,"E29.sketch_text.stroke-230"),sQuery(id+"F13.wireOp",EDGE,"E29.sketch_text.stroke-231"),sQuery(id+"F13.wireOp",EDGE,"E29.sketch_text.stroke-232"),sQuery(id+"F13.wireOp",EDGE,"E29.sketch_text.stroke-233")])]});
            var Q12;
            Q12=makeQuery(id+"F14.opExtrude","SWEPT_BODY",BODY,{"disambiguationData":[OSD([sQuery(id+"F13.wireOp",EDGE,"E29.sketch_text.stroke-234"),sQuery(id+"F13.wireOp",EDGE,"E29.sketch_text.stroke-235"),sQuery(id+"F13.wireOp",EDGE,"E29.sketch_text.stroke-236"),sQuery(id+"F13.wireOp",EDGE,"E29.sketch_text.stroke-237"),sQuery(id+"F13.wireOp",EDGE,"E29.sketch_text.stroke-238")])]});
            var Q13;
            Q13=makeQuery(id+"F14.opExtrude","SWEPT_BODY",BODY,{"disambiguationData":[OSD([sQuery(id+"F13.wireOp",EDGE,"E29.sketch_text.stroke-239"),sQuery(id+"F13.wireOp",EDGE,"E29.sketch_text.stroke-240"),sQuery(id+"F13.wireOp",EDGE,"E29.sketch_text.stroke-241"),sQuery(id+"F13.wireOp",EDGE,"E29.sketch_text.stroke-242")])]});
            var Q14;
            Q14=makeQuery(id+"F14.opExtrude","SWEPT_BODY",BODY,{"disambiguationData":[OSD([sQuery(id+"F13.wireOp",EDGE,"E29.sketch_text.stroke-243"),sQuery(id+"F13.wireOp",EDGE,"E29.sketch_text.stroke-244"),sQuery(id+"F13.wireOp",EDGE,"E29.sketch_text.stroke-245"),sQuery(id+"F13.wireOp",EDGE,"E29.sketch_text.stroke-246"),sQuery(id+"F13.wireOp",EDGE,"E29.sketch_text.stroke-247"),sQuery(id+"F13.wireOp",EDGE,"E29.sketch_text.stroke-248"),sQuery(id+"F13.wireOp",EDGE,"E29.sketch_text.stroke-249"),sQuery(id+"F13.wireOp",EDGE,"E29.sketch_text.stroke-250"),sQuery(id+"F13.wireOp",EDGE,"E29.sketch_text.stroke-251"),sQuery(id+"F13.wireOp",EDGE,"E29.sketch_text.stroke-252"),sQuery(id+"F13.wireOp",EDGE,"E29.sketch_text.stroke-253"),sQuery(id+"F13.wireOp",EDGE,"E29.sketch_text.stroke-254"),sQuery(id+"F13.wireOp",EDGE,"E29.sketch_text.stroke-255"),sQuery(id+"F13.wireOp",EDGE,"E29.sketch_text.stroke-256"),sQuery(id+"F13.wireOp",EDGE,"E29.sketch_text.stroke-257"),sQuery(id+"F13.wireOp",EDGE,"E29.sketch_text.stroke-258"),sQuery(id+"F13.wireOp",EDGE,"E29.sketch_text.stroke-259")])]});
            var Q15;
            Q15=makeQuery(id+"F14.opExtrude","SWEPT_BODY",BODY,{"disambiguationData":[OSD([sQuery(id+"F13.wireOp",EDGE,"E29.sketch_text.stroke-260"),sQuery(id+"F13.wireOp",EDGE,"E29.sketch_text.stroke-261"),sQuery(id+"F13.wireOp",EDGE,"E29.sketch_text.stroke-262"),sQuery(id+"F13.wireOp",EDGE,"E29.sketch_text.stroke-263"),sQuery(id+"F13.wireOp",EDGE,"E29.sketch_text.stroke-264"),sQuery(id+"F13.wireOp",EDGE,"E29.sketch_text.stroke-265"),sQuery(id+"F13.wireOp",EDGE,"E29.sketch_text.stroke-266"),sQuery(id+"F13.wireOp",EDGE,"E29.sketch_text.stroke-267"),sQuery(id+"F13.wireOp",EDGE,"E29.sketch_text.stroke-268"),sQuery(id+"F13.wireOp",EDGE,"E29.sketch_text.stroke-269"),sQuery(id+"F13.wireOp",EDGE,"E29.sketch_text.stroke-270"),sQuery(id+"F13.wireOp",EDGE,"E29.sketch_text.stroke-271"),sQuery(id+"F13.wireOp",EDGE,"E29.sketch_text.stroke-272"),sQuery(id+"F13.wireOp",EDGE,"E29.sketch_text.stroke-273"),sQuery(id+"F13.wireOp",EDGE,"E29.sketch_text.stroke-274"),sQuery(id+"F13.wireOp",EDGE,"E29.sketch_text.stroke-275"),sQuery(id+"F13.wireOp",EDGE,"E29.sketch_text.stroke-276"),sQuery(id+"F13.wireOp",EDGE,"E29.sketch_text.stroke-277"),sQuery(id+"F13.wireOp",EDGE,"E29.sketch_text.stroke-278"),sQuery(id+"F13.wireOp",EDGE,"E29.sketch_text.stroke-279")])]});
            var Q16;
            Q16=makeQuery(id+"F14.opExtrude","SWEPT_BODY",BODY,{"disambiguationData":[OSD([sQuery(id+"F13.wireOp",EDGE,"E29.sketch_text.stroke-280"),sQuery(id+"F13.wireOp",EDGE,"E29.sketch_text.stroke-281"),sQuery(id+"F13.wireOp",EDGE,"E29.sketch_text.stroke-282"),sQuery(id+"F13.wireOp",EDGE,"E29.sketch_text.stroke-283"),sQuery(id+"F13.wireOp",EDGE,"E29.sketch_text.stroke-284"),sQuery(id+"F13.wireOp",EDGE,"E29.sketch_text.stroke-285"),sQuery(id+"F13.wireOp",EDGE,"E29.sketch_text.stroke-286"),sQuery(id+"F13.wireOp",EDGE,"E29.sketch_text.stroke-287"),sQuery(id+"F13.wireOp",EDGE,"E29.sketch_text.stroke-288"),sQuery(id+"F13.wireOp",EDGE,"E29.sketch_text.stroke-289"),sQuery(id+"F13.wireOp",EDGE,"E29.sketch_text.stroke-290"),sQuery(id+"F13.wireOp",EDGE,"E29.sketch_text.stroke-291"),sQuery(id+"F13.wireOp",EDGE,"E29.sketch_text.stroke-292"),sQuery(id+"F13.wireOp",EDGE,"E29.sketch_text.stroke-293"),sQuery(id+"F13.wireOp",EDGE,"E29.sketch_text.stroke-294"),sQuery(id+"F13.wireOp",EDGE,"E29.sketch_text.stroke-295"),sQuery(id+"F13.wireOp",EDGE,"E29.sketch_text.stroke-296"),sQuery(id+"F13.wireOp",EDGE,"E29.sketch_text.stroke-297"),sQuery(id+"F13.wireOp",EDGE,"E29.sketch_text.stroke-298"),sQuery(id+"F13.wireOp",EDGE,"E29.sketch_text.stroke-299")])]});
            var Q17;
            Q17=makeQuery(id+"F14.opExtrude","SWEPT_BODY",BODY,{"disambiguationData":[OSD([sQuery(id+"F13.wireOp",EDGE,"E29.sketch_text.stroke-300"),sQuery(id+"F13.wireOp",EDGE,"E29.sketch_text.stroke-301"),sQuery(id+"F13.wireOp",EDGE,"E29.sketch_text.stroke-302"),sQuery(id+"F13.wireOp",EDGE,"E29.sketch_text.stroke-303"),sQuery(id+"F13.wireOp",EDGE,"E29.sketch_text.stroke-304"),sQuery(id+"F13.wireOp",EDGE,"E29.sketch_text.stroke-305"),sQuery(id+"F13.wireOp",EDGE,"E29.sketch_text.stroke-306"),sQuery(id+"F13.wireOp",EDGE,"E29.sketch_text.stroke-307"),sQuery(id+"F13.wireOp",EDGE,"E29.sketch_text.stroke-308"),sQuery(id+"F13.wireOp",EDGE,"E29.sketch_text.stroke-309"),sQuery(id+"F13.wireOp",EDGE,"E29.sketch_text.stroke-310"),sQuery(id+"F13.wireOp",EDGE,"E29.sketch_text.stroke-311"),sQuery(id+"F13.wireOp",EDGE,"E29.sketch_text.stroke-312")])]});
            var Q18;
            Q18=makeQuery(id+"F14.opExtrude","SWEPT_BODY",BODY,{"disambiguationData":[OSD([sQuery(id+"F13.wireOp",EDGE,"E29.sketch_text.stroke-313"),sQuery(id+"F13.wireOp",EDGE,"E29.sketch_text.stroke-314"),sQuery(id+"F13.wireOp",EDGE,"E29.sketch_text.stroke-315"),sQuery(id+"F13.wireOp",EDGE,"E29.sketch_text.stroke-316"),sQuery(id+"F13.wireOp",EDGE,"E29.sketch_text.stroke-317")])]});
            var Q19;
            Q19=makeQuery(id+"F14.opExtrude","SWEPT_BODY",BODY,{"disambiguationData":[OSD([sQuery(id+"F13.wireOp",EDGE,"E29.sketch_text.stroke-318"),sQuery(id+"F13.wireOp",EDGE,"E29.sketch_text.stroke-319"),sQuery(id+"F13.wireOp",EDGE,"E29.sketch_text.stroke-320"),sQuery(id+"F13.wireOp",EDGE,"E29.sketch_text.stroke-321")])]});
            var Q20;
            Q20=makeQuery(id+"F14.opExtrude","SWEPT_BODY",BODY,{"disambiguationData":[OSD([sQuery(id+"F13.wireOp",EDGE,"E29.sketch_text.stroke-322"),sQuery(id+"F13.wireOp",EDGE,"E29.sketch_text.stroke-323"),sQuery(id+"F13.wireOp",EDGE,"E29.sketch_text.stroke-324"),sQuery(id+"F13.wireOp",EDGE,"E29.sketch_text.stroke-325"),sQuery(id+"F13.wireOp",EDGE,"E29.sketch_text.stroke-326"),sQuery(id+"F13.wireOp",EDGE,"E29.sketch_text.stroke-327"),sQuery(id+"F13.wireOp",EDGE,"E29.sketch_text.stroke-328"),sQuery(id+"F13.wireOp",EDGE,"E29.sketch_text.stroke-329"),sQuery(id+"F13.wireOp",EDGE,"E29.sketch_text.stroke-330"),sQuery(id+"F13.wireOp",EDGE,"E29.sketch_text.stroke-331"),sQuery(id+"F13.wireOp",EDGE,"E29.sketch_text.stroke-332"),sQuery(id+"F13.wireOp",EDGE,"E29.sketch_text.stroke-333"),sQuery(id+"F13.wireOp",EDGE,"E29.sketch_text.stroke-334"),sQuery(id+"F13.wireOp",EDGE,"E29.sketch_text.stroke-335"),sQuery(id+"F13.wireOp",EDGE,"E29.sketch_text.stroke-336"),sQuery(id+"F13.wireOp",EDGE,"E29.sketch_text.stroke-337"),sQuery(id+"F13.wireOp",EDGE,"E29.sketch_text.stroke-338")])]});
            var Q21;
            Q21=makeQuery(id+"F14.opExtrude","SWEPT_BODY",BODY,{"disambiguationData":[OSD([sQuery(id+"F13.wireOp",EDGE,"E29.sketch_text.stroke-339"),sQuery(id+"F13.wireOp",EDGE,"E29.sketch_text.stroke-340"),sQuery(id+"F13.wireOp",EDGE,"E29.sketch_text.stroke-341"),sQuery(id+"F13.wireOp",EDGE,"E29.sketch_text.stroke-342"),sQuery(id+"F13.wireOp",EDGE,"E29.sketch_text.stroke-343"),sQuery(id+"F13.wireOp",EDGE,"E29.sketch_text.stroke-344"),sQuery(id+"F13.wireOp",EDGE,"E29.sketch_text.stroke-345"),sQuery(id+"F13.wireOp",EDGE,"E29.sketch_text.stroke-346"),sQuery(id+"F13.wireOp",EDGE,"E29.sketch_text.stroke-347"),sQuery(id+"F13.wireOp",EDGE,"E29.sketch_text.stroke-348"),sQuery(id+"F13.wireOp",EDGE,"E29.sketch_text.stroke-349"),sQuery(id+"F13.wireOp",EDGE,"E29.sketch_text.stroke-350"),sQuery(id+"F13.wireOp",EDGE,"E29.sketch_text.stroke-351"),sQuery(id+"F13.wireOp",EDGE,"E29.sketch_text.stroke-352"),sQuery(id+"F13.wireOp",EDGE,"E29.sketch_text.stroke-353"),sQuery(id+"F13.wireOp",EDGE,"E29.sketch_text.stroke-354"),sQuery(id+"F13.wireOp",EDGE,"E29.sketch_text.stroke-355"),sQuery(id+"F13.wireOp",EDGE,"E29.sketch_text.stroke-356"),sQuery(id+"F13.wireOp",EDGE,"E29.sketch_text.stroke-357"),sQuery(id+"F13.wireOp",EDGE,"E29.sketch_text.stroke-358"),sQuery(id+"F13.wireOp",EDGE,"E29.sketch_text.stroke-359"),sQuery(id+"F13.wireOp",EDGE,"E29.sketch_text.stroke-360"),sQuery(id+"F13.wireOp",EDGE,"E29.sketch_text.stroke-361"),sQuery(id+"F13.wireOp",EDGE,"E29.sketch_text.stroke-362"),sQuery(id+"F13.wireOp",EDGE,"E29.sketch_text.stroke-363"),sQuery(id+"F13.wireOp",EDGE,"E29.sketch_text.stroke-364"),sQuery(id+"F13.wireOp",EDGE,"E29.sketch_text.stroke-365"),sQuery(id+"F13.wireOp",EDGE,"E29.sketch_text.stroke-366"),sQuery(id+"F13.wireOp",EDGE,"E29.sketch_text.stroke-367"),sQuery(id+"F13.wireOp",EDGE,"E29.sketch_text.stroke-368"),sQuery(id+"F13.wireOp",EDGE,"E29.sketch_text.stroke-369"),sQuery(id+"F13.wireOp",EDGE,"E29.sketch_text.stroke-370"),sQuery(id+"F13.wireOp",EDGE,"E29.sketch_text.stroke-371"),sQuery(id+"F13.wireOp",EDGE,"E29.sketch_text.stroke-372"),sQuery(id+"F13.wireOp",EDGE,"E29.sketch_text.stroke-373"),sQuery(id+"F13.wireOp",EDGE,"E29.sketch_text.stroke-374"),sQuery(id+"F13.wireOp",EDGE,"E29.sketch_text.stroke-375"),sQuery(id+"F13.wireOp",EDGE,"E29.sketch_text.stroke-376"),sQuery(id+"F13.wireOp",EDGE,"E29.sketch_text.stroke-377"),sQuery(id+"F13.wireOp",EDGE,"E29.sketch_text.stroke-378"),sQuery(id+"F13.wireOp",EDGE,"E29.sketch_text.stroke-379"),sQuery(id+"F13.wireOp",EDGE,"E29.sketch_text.stroke-380"),sQuery(id+"F13.wireOp",EDGE,"E29.sketch_text.stroke-381"),sQuery(id+"F13.wireOp",EDGE,"E29.sketch_text.stroke-382")])]});
            var Q22;
            Q22=makeQuery(id+"F1.opExtrude","SWEPT_BODY",BODY,{"disambiguationData":[OSD([sQuery(id+"F0.wireOp",EDGE,"E0.bottom"),sQuery(id+"F0.wireOp",EDGE,"E0.top"),sQuery(id+"F0.wireOp",EDGE,"E1"),sQuery(id+"F0.wireOp",EDGE,"E2")])]});
            booleanBodies(context, id + "F17", {"operationType" : BooleanOperationType.SUBTRACTION, "tools" : qUnion([Q0, Q1, Q2, Q3, Q4, Q5, Q6, Q7, Q8, Q9, Q10, Q11, Q12, Q13, Q14, Q15, Q16, Q17, Q18, Q19, Q20, Q21]), "targets" : qUnion([Q22]), "keepTools" : true});
        }
        {
            var Q0;
            Q0=makeQuery(id+"F10.opExtrude","SWEPT_BODY",BODY,{"disambiguationData":[OSD([sQuery(id+"F9.wireOp",EDGE,"E17")])]});
            var Q1;
            Q1=makeQuery(id+"F1.opExtrude","SWEPT_BODY",BODY,{"disambiguationData":[OSD([sQuery(id+"F0.wireOp",EDGE,"E0.bottom"),sQuery(id+"F0.wireOp",EDGE,"E0.top"),sQuery(id+"F0.wireOp",EDGE,"E1"),sQuery(id+"F0.wireOp",EDGE,"E2")])]});
            booleanBodies(context, id + "F18", {"operationType" : BooleanOperationType.SUBTRACTION, "tools" : qUnion([Q0]), "targets" : qUnion([Q1]), "keepTools" : true});
        }
        {
            var Q0;
            Q0=makeQuery(id+"F6.opExtrude","SWEPT_BODY",BODY,{"disambiguationData":[OSD([sQuery(id+"F5.wireOp",EDGE,"E11"),sQuery(id+"F5.wireOp",EDGE,"E12"),sQuery(id+"F5.wireOp",EDGE,"E13.bottom"),sQuery(id+"F5.wireOp",EDGE,"E13.top")])]});
            var Q1;
            Q1=makeQuery(id+"F1.opExtrude","SWEPT_BODY",BODY,{"disambiguationData":[OSD([sQuery(id+"F0.wireOp",EDGE,"E0.bottom"),sQuery(id+"F0.wireOp",EDGE,"E0.top"),sQuery(id+"F0.wireOp",EDGE,"E1"),sQuery(id+"F0.wireOp",EDGE,"E2")])]});
            booleanBodies(context, id + "F19", {"operationType" : BooleanOperationType.SUBTRACTION, "tools" : qUnion([Q0]), "targets" : qUnion([Q1]), "keepTools" : true});
        }
        {
            var Q0;
            Q0=makeQuery(id+"F8.opExtrude","SWEPT_BODY",BODY,{"disambiguationData":[OSD([sQuery(id+"F7.wireOp",EDGE,"E14"),sQuery(id+"F7.wireOp",EDGE,"E15"),sQuery(id+"F7.wireOp",EDGE,"E16.bottom"),sQuery(id+"F7.wireOp",EDGE,"E16.top")])]});
            var Q1;
            Q1=makeQuery(id+"F1.opExtrude","SWEPT_BODY",BODY,{"disambiguationData":[OSD([sQuery(id+"F0.wireOp",EDGE,"E0.bottom"),sQuery(id+"F0.wireOp",EDGE,"E0.top"),sQuery(id+"F0.wireOp",EDGE,"E1"),sQuery(id+"F0.wireOp",EDGE,"E2")])]});
            booleanBodies(context, id + "F20", {"operationType" : BooleanOperationType.SUBTRACTION, "tools" : qUnion([Q0]), "targets" : qUnion([Q1]), "keepTools" : true});
        }
        {
            var Q0;
            Q0=qCreatedBy(makeId("Top.planeOp"),FACE);
            var sketch = newSketch(context, id + "F21", { "sketchPlane" : qUnion([Q0])});
            skCircle(sketch, "E30.MirrorC", {"center": v(-46, 0) * mm, "radius": 2.75 * mm});
            skSolve(sketch);
        }
        {
            var Q0;
            Q0=qSketchRegion(id+"F21",true);
            extrude(context, id + "F22", {"entities" : qUnion([Q0]), "operationType" : NewBodyOperationType.REMOVE, "endBound" : BoundingType.THROUGH_ALL, "depth" : 25 * mm});
        }
    });
